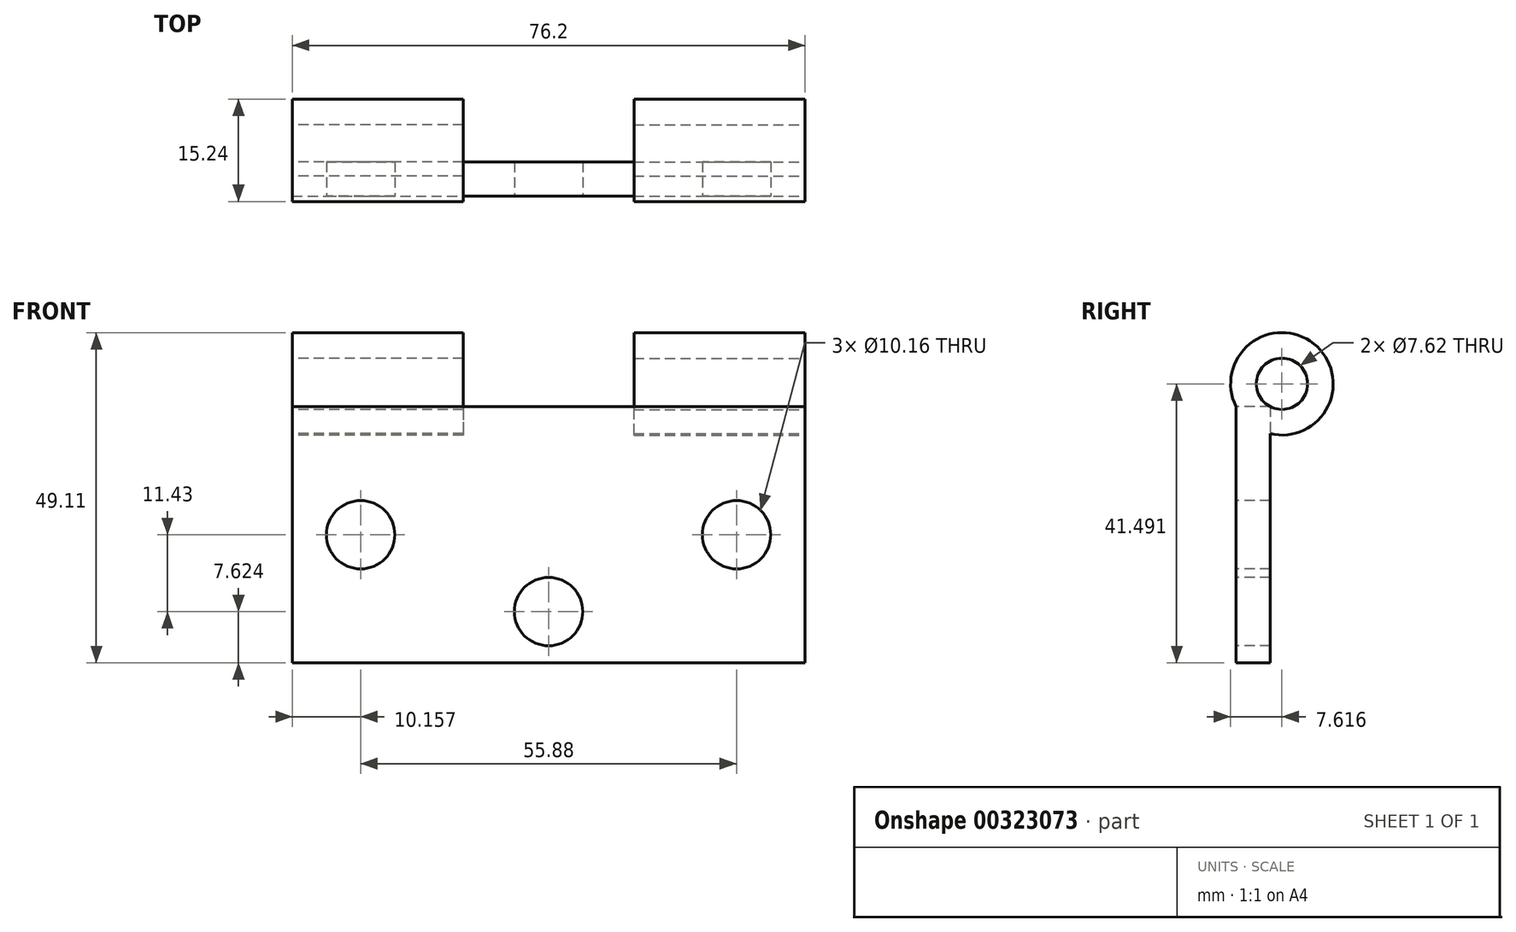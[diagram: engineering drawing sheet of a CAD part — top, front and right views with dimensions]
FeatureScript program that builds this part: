
annotation { "Feature Type Name" : "Feature", "Feature Type Description" : "" }
export const myFeature = defineFeature(function(context is Context, id is Id, definition is map)
    precondition{}
    {
        {
            var Q0;
            Q0=qCreatedBy(makeId("Front.planeOp"),FACE);
            var sketch = newSketch(context, id + "F0", { "sketchPlane" : qUnion([Q0])});
            skLineSegment(sketch, "E0.bottom", {"start": v(-60.18, 6.44) * mm, "end": v(16.02, 6.44) * mm});
            skLineSegment(sketch, "E0.top", {"start": v(-60.18, -31.66) * mm, "end": v(16.02, -31.66) * mm});
            skLineSegment(sketch, "E0.left", {"start": v(-60.18, 6.44) * mm, "end": v(-60.18, -31.66) * mm});
            skLineSegment(sketch, "E0.right", {"start": v(16.02, 6.44) * mm, "end": v(16.02, -31.66) * mm});
            skSolve(sketch);
        }
        {
            var Q0;
            Q0 = qSketchRegion(id + "F0", true);
            var Q1;
            Q1 = qSketchRegion(id + "F2", true);
            extrude(context, id + "F1", {"entities" : qUnion([Q0, Q1]), "depth" : 5.08 * mm});
        }
        {
            var Q0;
            Q0=makeQuery(id+"F1.opExtrude","SWEPT_FACE",FACE,{"disambiguationData":[OSD([sQuery(id+"F0.wireOp",EDGE,"E0.right")])]});
            var sketch = newSketch(context, id + "F2", { "sketchPlane" : qUnion([Q0])});
            skCircle(sketch, "E1", {"center": v(1.75, 9.83) * mm, "radius": 3.81 * mm});
            skCircle(sketch, "E2", {"center": v(1.75, 9.83) * mm, "radius": 7.62 * mm});
            skSolve(sketch);
        }
        {
            var Q0;
            Q0 = qSketchRegion(id + "F2", true);
            extrude(context, id + "F3", {"entities" : qUnion([Q0]), "operationType" : NewBodyOperationType.ADD, "oppositeDirection" : true, "depth" : 25.4 * mm});
        }
        {
            var Q0;
            Q0=makeQuery(id+"F1.opExtrude","SWEPT_FACE",FACE,{"disambiguationData":[OSD([sQuery(id+"F0.wireOp",EDGE,"E0.left")])]});
            var sketch = newSketch(context, id + "F4", { "sketchPlane" : qUnion([Q0])});
            skCircle(sketch, "E3", {"center": v(-1.75, 9.83) * mm, "radius": 3.81 * mm});
            skCircle(sketch, "E4", {"center": v(-1.75, 9.83) * mm, "radius": 7.62 * mm});
            skSolve(sketch);
        }
        {
            var Q0;
            Q0 = qSketchRegion(id + "F4", true);
            extrude(context, id + "F5", {"entities" : qUnion([Q0]), "operationType" : NewBodyOperationType.ADD, "oppositeDirection" : true, "depth" : 25.4 * mm});
        }
        {
            var Q0;
            Q0=makeQuery(id+"F1.opExtrude","CAP_FACE",FACE,{"disambiguationData":[OSD([sQuery(id+"F0.wireOp",EDGE,"E0.bottom"),sQuery(id+"F0.wireOp",EDGE,"E0.top"),sQuery(id+"F0.wireOp",EDGE,"E0.left"),sQuery(id+"F0.wireOp",EDGE,"E0.right")])],"isStart":false});
            var sketch = newSketch(context, id + "F6", { "sketchPlane" : qUnion([Q0])});
            skCircle(sketch, "E5", {"center": v(-50.02, -12.6) * mm, "radius": 5.08 * mm});
            skCircle(sketch, "E6", {"center": v(-22.08, -24.04) * mm, "radius": 5.08 * mm});
            skCircle(sketch, "E7", {"center": v(5.86, -12.6) * mm, "radius": 5.08 * mm});
            skSolve(sketch);
        }
        {
            var Q0;
            Q0 = qSketchRegion(id + "F6", true);
            extrude(context, id + "F7", {"entities" : qUnion([Q0]), "operationType" : NewBodyOperationType.REMOVE, "endBound" : BoundingType.UP_TO_NEXT, "oppositeDirection" : true, "depth" : 25.4 * mm});
        }
    });
